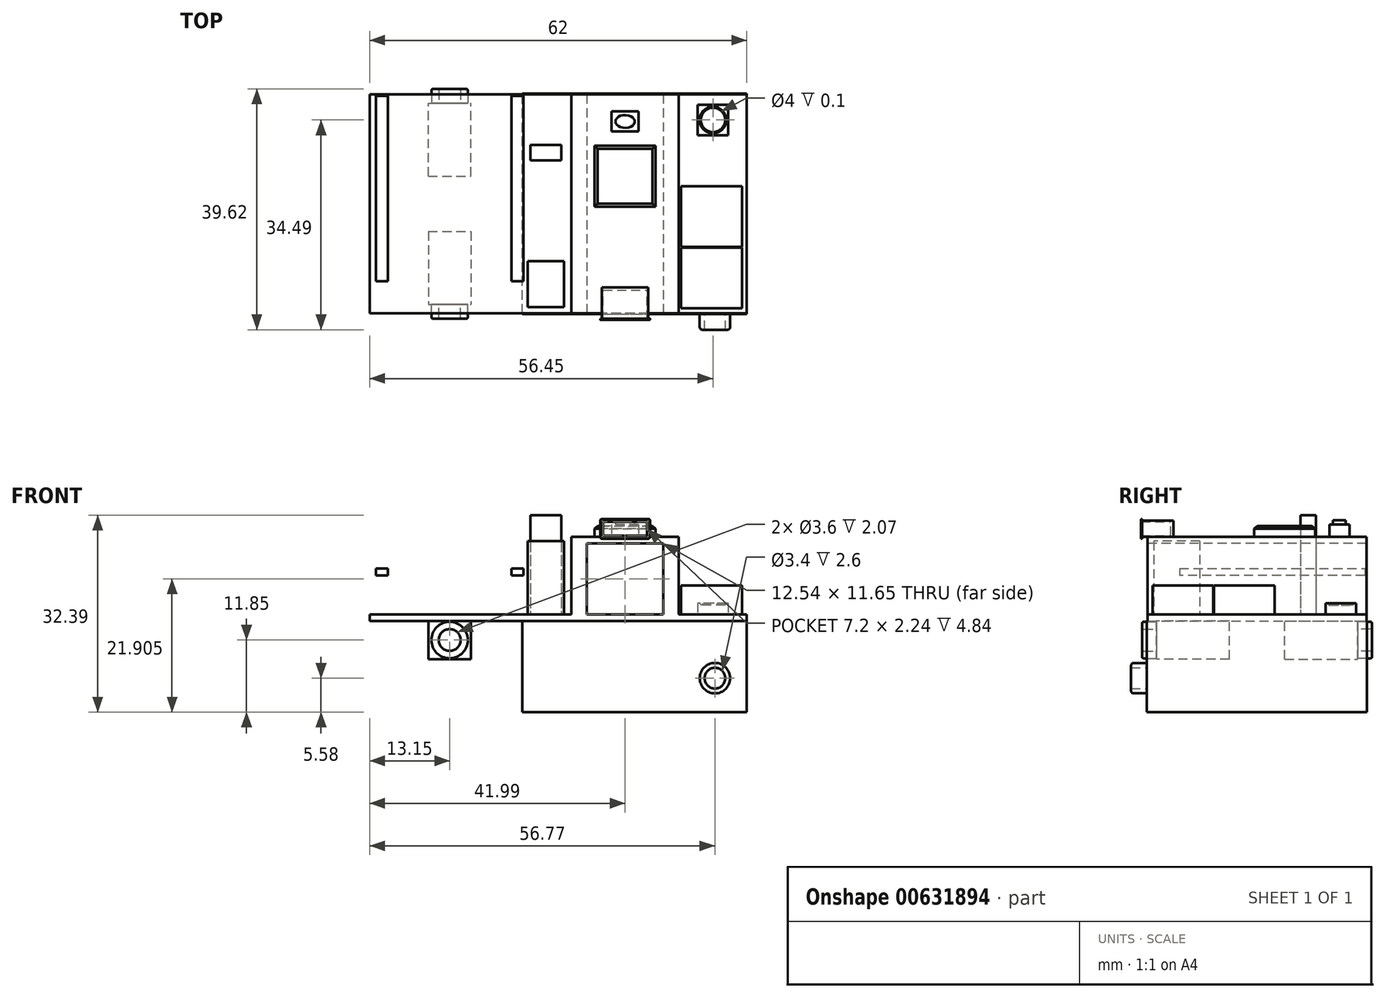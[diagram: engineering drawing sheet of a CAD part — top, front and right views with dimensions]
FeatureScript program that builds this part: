
annotation { "Feature Type Name" : "Feature", "Feature Type Description" : "" }
export const myFeature = defineFeature(function(context is Context, id is Id, definition is map)
    precondition{}
    {
        {
            assignVariable(context, id + "F0", {"name" : "epaisseur", "anyValue" : 1.08});
        }
        {
            var Q0;
            Q0=qCreatedBy(makeId("Top.planeOp"),FACE);
            var sketch = newSketch(context, id + "F1", { "sketchPlane" : qUnion([Q0])});
            skLineSegment(sketch, "E0.bottom", {"start": v(31, -18) * mm, "end": v(-31, -18) * mm});
            skLineSegment(sketch, "E0.top", {"start": v(31, 18) * mm, "end": v(-31, 18) * mm});
            skLineSegment(sketch, "E0.left", {"start": v(31, -18) * mm, "end": v(31, 18) * mm});
            skLineSegment(sketch, "E0.right", {"start": v(-31, -18) * mm, "end": v(-31, 18) * mm});
            skPoint(sketch, "E0.middle", {"position": v(0, 0) * mm});
            skSolve(sketch);
        }
        {
            var Q0;
            Q0=qSketchRegion(id+"F1",true);
            extrude(context, id + "F2", {"entities" : qUnion([Q0]), "depth" : (getVariable(context, 'epaisseur') / 2) * mm, "offsetDistance" : 25 * mm, "hasSecondDirection" : true, "secondDirectionOppositeDirection" : true, "secondDirectionDepth" : (getVariable(context, 'epaisseur') / 2) * mm});
        }
        {
            var Q0;
            Q0=makeQuery(id+"F2.opExtrude","CAP_FACE",FACE,{"disambiguationData":[OSD([sQuery(id+"F1.wireOp",EDGE,"E0.bottom"),sQuery(id+"F1.wireOp",EDGE,"E0.top"),sQuery(id+"F1.wireOp",EDGE,"E0.left"),sQuery(id+"F1.wireOp",EDGE,"E0.right")])],"isStart":false});
            var sketch = newSketch(context, id + "F3", { "sketchPlane" : qUnion([Q0])});
            skLineSegment(sketch, "E1.bottom", {"start": v(27.95, 11.3) * mm, "end": v(22.95, 11.3) * mm});
            skLineSegment(sketch, "E1.top", {"start": v(27.95, 16.3) * mm, "end": v(22.95, 16.3) * mm});
            skLineSegment(sketch, "E1.left", {"start": v(27.95, 11.3) * mm, "end": v(27.95, 16.3) * mm});
            skLineSegment(sketch, "E1.right", {"start": v(22.95, 11.3) * mm, "end": v(22.95, 16.3) * mm});
            skPoint(sketch, "E1.middle", {"position": v(25.45, 13.8) * mm});
            skCircle(sketch, "E2", {"center": v(25.45, 13.8) * mm, "radius": 2 * mm});
            skLineSegment(sketch, "E3.bottom", {"start": v(19.8, -18) * mm, "end": v(2.18, -18) * mm});
            skLineSegment(sketch, "E3.top", {"start": v(19.8, 18) * mm, "end": v(2.18, 18) * mm});
            skLineSegment(sketch, "E3.left", {"start": v(19.8, -18) * mm, "end": v(19.8, 18) * mm});
            skLineSegment(sketch, "E3.right", {"start": v(2.18, -18) * mm, "end": v(2.18, 18) * mm});
            skLineSegment(sketch, "E4", {"start": v(4.72, 18) * mm, "end": v(4.72, -18) * mm});
            skLineSegment(sketch, "E5", {"start": v(17.26, 18) * mm, "end": v(17.26, -18) * mm});
            skLineSegment(sketch, "E6.bottom", {"start": v(30.2, 2.9) * mm, "end": v(20.2, 2.9) * mm});
            skLineSegment(sketch, "E6.top", {"start": v(30.2, -7.1) * mm, "end": v(20.2, -7.1) * mm});
            skLineSegment(sketch, "E6.left", {"start": v(30.2, 2.9) * mm, "end": v(30.2, -7.1) * mm});
            skLineSegment(sketch, "E6.right", {"start": v(20.2, 2.9) * mm, "end": v(20.2, -7.1) * mm});
            skLineSegment(sketch, "E7.1.0.0", {"start": v(30.2, -7.2) * mm, "end": v(20.2, -7.2) * mm});
            skLineSegment(sketch, "E7.1.0.1", {"start": v(30.2, -17.2) * mm, "end": v(20.2, -17.2) * mm});
            skLineSegment(sketch, "E7.1.0.2", {"start": v(30.2, -7.2) * mm, "end": v(30.2, -17.2) * mm});
            skLineSegment(sketch, "E7.1.0.3", {"start": v(20.2, -7.2) * mm, "end": v(20.2, -17.2) * mm});
            skLineSegment(sketch, "E7.direction1", {"start": v(20.2, -7.1) * mm, "end": v(20.2, -17.2) * mm, "construction": true});
            skLineSegment(sketch, "E8", {"start": v(-30, 17.75) * mm, "end": v(-5.7, 17.75) * mm});
            skLineSegment(sketch, "E9", {"start": v(-5.7, 17.75) * mm, "end": v(-5.7, -12.75) * mm});
            skLineSegment(sketch, "E10", {"start": v(-5.7, -12.75) * mm, "end": v(-13.35, -17.75) * mm});
            skLineSegment(sketch, "E11", {"start": v(-13.35, -17.75) * mm, "end": v(-22.35, -17.75) * mm});
            skLineSegment(sketch, "E12", {"start": v(-22.35, -17.75) * mm, "end": v(-30, -12.75) * mm});
            skLineSegment(sketch, "E13", {"start": v(-30, -12.75) * mm, "end": v(-30, 17.75) * mm});
            skLineSegment(sketch, "E14.bottom", {"start": v(-30, 17.75) * mm, "end": v(-28, 17.75) * mm});
            skLineSegment(sketch, "E14.top", {"start": v(-30, -12.75) * mm, "end": v(-28, -12.75) * mm});
            skLineSegment(sketch, "E14.left", {"start": v(-30, 17.75) * mm, "end": v(-30, -12.75) * mm});
            skLineSegment(sketch, "E14.right", {"start": v(-28, 17.75) * mm, "end": v(-28, -12.75) * mm});
            skLineSegment(sketch, "E15.bottom", {"start": v(-5.7, 17.75) * mm, "end": v(-7.7, 17.75) * mm});
            skLineSegment(sketch, "E15.top", {"start": v(-5.7, -12.75) * mm, "end": v(-7.7, -12.75) * mm});
            skLineSegment(sketch, "E15.right", {"start": v(-7.7, 17.75) * mm, "end": v(-7.7, -12.75) * mm});
            skLineSegment(sketch, "E16.bottom", {"start": v(-5.02, -9.4) * mm, "end": v(0.98, -9.4) * mm});
            skLineSegment(sketch, "E16.top", {"start": v(-5.02, -17) * mm, "end": v(0.98, -17) * mm});
            skLineSegment(sketch, "E16.left", {"start": v(-5.02, -9.4) * mm, "end": v(-5.02, -17) * mm});
            skLineSegment(sketch, "E16.right", {"start": v(0.98, -9.4) * mm, "end": v(0.98, -17) * mm});
            skCircle(sketch, "E17", {"center": v(-1.12, 15.47) * mm, "radius": 2 * mm});
            skLineSegment(sketch, "E18.bottom", {"start": v(-4.55, 9.7) * mm, "end": v(0.53, 9.7) * mm});
            skLineSegment(sketch, "E18.top", {"start": v(-4.55, 7.15) * mm, "end": v(0.53, 7.15) * mm});
            skLineSegment(sketch, "E18.left", {"start": v(-4.55, 9.7) * mm, "end": v(-4.55, 7.15) * mm});
            skLineSegment(sketch, "E18.right", {"start": v(0.53, 9.7) * mm, "end": v(0.53, 7.15) * mm});
            skSolve(sketch);
        }
        {
            var Q0;
            Q0=makeQuery(id+"F3.imprint","IMPRINT",FACE,{"disambiguationData":[TD([[makeQuery(id+"F3.imprint","IMPRINT",EDGE,{"derivedFrom":sQuery(id+"F3.wireOp",EDGE,"E1.bottom")}),-1.0]])]});
            var Q1;
            Q1=makeQuery(id+"F3.imprint","IMPRINT",FACE,{"disambiguationData":[TD([[makeQuery(id+"F3.imprint","IMPRINT",EDGE,{"derivedFrom":sQuery(id+"F3.wireOp",EDGE,"46dbcd92-cdc2-429d-924f-770beef507a0.1.1.0")}),-1.0]])]});
            var Q2;
            Q2=makeQuery(id+"F3.imprint","IMPRINT",FACE,{"disambiguationData":[TD([[makeQuery(id+"F3.imprint","IMPRINT",EDGE,{"derivedFrom":sQuery(id+"F3.wireOp",EDGE,"25c404a9-2ccf-4400-a537-ff987a43f8d3.1.0.0")}),-1.0]])]});
            var Q3;
            Q3=makeQuery(id+"F3.imprint","IMPRINT",FACE,{"disambiguationData":[TD([[makeQuery(id+"F3.imprint","IMPRINT",EDGE,{"derivedFrom":sQuery(id+"F3.wireOp",EDGE,"5cae1187-fbfc-416b-a3f4-cd89fc04e58b.1.0.1")}),1.0]])]});
            var Q4;
            Q4=makeQuery(id+"F3.imprint","IMPRINT",FACE,{"disambiguationData":[TD([[makeQuery(id+"F3.imprint","IMPRINT",EDGE,{"derivedFrom":sQuery(id+"F3.wireOp",EDGE,"5cae1187-fbfc-416b-a3f4-cd89fc04e58b.1.0.7")}),-1.0]])]});
            extrude(context, id + "F4", {"entities" : qUnion([Q0, Q1, Q2, Q3, Q4]), "operationType" : NewBodyOperationType.ADD, "depth" : 1.8 * mm, "offsetDistance" : 25 * mm});
        }
        {
            var Q0;
            Q0=makeQuery(id+"F3.imprint","IMPRINT",FACE,{"disambiguationData":[TD([[makeQuery(id+"F3.imprint","IMPRINT",EDGE,{"derivedFrom":sQuery(id+"F3.wireOp",EDGE,"25c404a9-2ccf-4400-a537-ff987a43f8d3.1.0.4")}),1.0]])]});
            var Q1;
            Q1=makeQuery(id+"F3.imprint","IMPRINT",FACE,{"disambiguationData":[TD([[makeQuery(id+"F3.imprint","IMPRINT",EDGE,{"derivedFrom":sQuery(id+"F3.wireOp",EDGE,"46dbcd92-cdc2-429d-924f-770beef507a0.13.1.0")}),1.0]])]});
            var Q2;
            Q2=makeQuery(id+"F3.imprint","IMPRINT",FACE,{"disambiguationData":[TD([[makeQuery(id+"F3.imprint","IMPRINT",EDGE,{"derivedFrom":sQuery(id+"F3.wireOp",EDGE,"5cae1187-fbfc-416b-a3f4-cd89fc04e58b.1.0.6")}),1.0]])]});
            var Q3;
            Q3=makeQuery(id+"F3.imprint","IMPRINT",FACE,{"disambiguationData":[TD([[makeQuery(id+"F3.imprint","IMPRINT",EDGE,{"derivedFrom":sQuery(id+"F3.wireOp",EDGE,"5cae1187-fbfc-416b-a3f4-cd89fc04e58b.1.0.10")}),1.0]])]});
            var Q4;
            Q4=makeQuery(id+"F3.imprint","IMPRINT",FACE,{"disambiguationData":[TD([[makeQuery(id+"F3.imprint","IMPRINT",EDGE,{"derivedFrom":sQuery(id+"F3.wireOp",EDGE,"E2")}),1.0]])]});
            extrude(context, id + "F5", {"entities" : qUnion([Q0, Q1, Q2, Q3, Q4]), "operationType" : NewBodyOperationType.ADD, "depth" : 1.5 * mm, "offsetDistance" : 25 * mm});
        }
        {
            var Q0;
            Q0=makeQuery(id+"F4.opExtrude","CAP_EDGE",EDGE,{"disambiguationData":[OSD([sQuery(id+"F3.wireOp",EDGE,"5cae1187-fbfc-416b-a3f4-cd89fc04e58b.1.0.6")])],"isStart":false});
            var Q1;
            Q1=makeQuery(id+"F4.opExtrude","CAP_EDGE",EDGE,{"disambiguationData":[OSD([sQuery(id+"F3.wireOp",EDGE,"5cae1187-fbfc-416b-a3f4-cd89fc04e58b.1.0.10")])],"isStart":false});
            var Q2;
            Q2=makeQuery(id+"F4.opExtrude","CAP_EDGE",EDGE,{"disambiguationData":[OSD([sQuery(id+"F3.wireOp",EDGE,"E2")])],"isStart":false});
            var Q3;
            Q3=makeQuery(id+"F4.opExtrude","CAP_EDGE",EDGE,{"disambiguationData":[OSD([sQuery(id+"F3.wireOp",EDGE,"25c404a9-2ccf-4400-a537-ff987a43f8d3.1.0.4")])],"isStart":false});
            var Q4;
            Q4=makeQuery(id+"F4.opExtrude","CAP_EDGE",EDGE,{"disambiguationData":[OSD([sQuery(id+"F3.wireOp",EDGE,"46dbcd92-cdc2-429d-924f-770beef507a0.13.1.0")])],"isStart":false});
            chamfer(context, id + "F6", {"entities" : qUnion([Q0, Q1, Q2, Q3, Q4]), "width" : 0.2 * mm, "tangentPropagation" : true});
        }
        {
            var Q0;
            {var subQ0=sQuery(id+"F3.wireOp",EDGE,"E3.right");Q0=makeQuery(id+"F3.imprint","IMPRINT",FACE,{"disambiguationData":[TD([[makeQuery(id+"F3.imprint","IMPRINT",EDGE,{"derivedFrom":subQ0}),-1.0]])]});}
            var Q1;
            {var subQ0=sQuery(id+"F3.wireOp",EDGE,"fOPfJSet-owwX-ZUtX-Vyne-BZuTA3JeBzhn");Q1=makeQuery(id+"F3.imprint","IMPRINT",FACE,{"disambiguationData":[TD([[makeQuery(id+"F3.imprint","IMPRINT",EDGE,{"derivedFrom":subQ0}),1.0]])]});}
            var Q2;
            {var subQ0=sQuery(id+"F3.wireOp",EDGE,"E3.left");Q2=makeQuery(id+"F3.imprint","IMPRINT",FACE,{"disambiguationData":[TD([[makeQuery(id+"F3.imprint","IMPRINT",EDGE,{"derivedFrom":subQ0}),1.0]])]});}
            var Q3;
            {var subQ0=sQuery(id+"F3.wireOp",EDGE,"E4");Q3=makeQuery(id+"F3.imprint","IMPRINT",FACE,{"disambiguationData":[TD([[makeQuery(id+"F3.imprint","IMPRINT",EDGE,{"derivedFrom":subQ0}),1.0]])]});}
            extrude(context, id + "F7", {"entities" : qUnion([Q0, Q1, Q2, Q3]), "operationType" : NewBodyOperationType.ADD, "depth" : 12.75 * mm, "offsetDistance" : 25 * mm});
        }
        {
            var Q0;
            {var subQ0=sQuery(id+"F3.wireOp",EDGE,"E4");Q0=makeQuery(id+"F3.imprint","IMPRINT",FACE,{"disambiguationData":[TD([[makeQuery(id+"F3.imprint","IMPRINT",EDGE,{"derivedFrom":subQ0}),1.0]])]});}
            var Q1;
            Q1=makeQuery(id+"F7.opExtrude","CAP_FACE",FACE,{"disambiguationData":[OSD([sQuery(id+"F3.wireOp",EDGE,"E3.bottom"),sQuery(id+"F3.wireOp",EDGE,"E3.top"),sQuery(id+"F3.wireOp",EDGE,"E3.left"),sQuery(id+"F3.wireOp",EDGE,"E3.right")])],"isStart":false});
            extrude(context, id + "F8", {"entities" : qUnion([Q0]), "operationType" : NewBodyOperationType.REMOVE, "endBound" : BoundingType.UP_TO_SURFACE, "depth" : 25 * mm, "endBoundEntityFace" : qUnion([Q1]), "hasOffset" : true, "offsetDistance" : 1.1 * mm});
        }
        {
            var Q0;
            Q0=makeQuery(id+"F3.imprint","IMPRINT",FACE,{"disambiguationData":[TD([[makeQuery(id+"F3.imprint","IMPRINT",EDGE,{"derivedFrom":sQuery(id+"F3.wireOp",EDGE,"E7.1.0.0")}),1.0]])]});
            var Q1;
            Q1=makeQuery(id+"F3.imprint","IMPRINT",FACE,{"disambiguationData":[TD([[makeQuery(id+"F3.imprint","IMPRINT",EDGE,{"derivedFrom":sQuery(id+"F3.wireOp",EDGE,"E6.bottom")}),1.0]])]});
            extrude(context, id + "F9", {"entities" : qUnion([Q0, Q1]), "operationType" : NewBodyOperationType.ADD, "depth" : 4.75 * mm, "offsetDistance" : 25 * mm});
        }
        {
            var Q0;
            Q0=makeQuery(id+"F3.imprint","IMPRINT",FACE,{"disambiguationData":[TD([[makeQuery(id+"F3.imprint","IMPRINT",EDGE,{"derivedFrom":sQuery(id+"F3.wireOp",EDGE,"E14.bottom")}),-1.0]])]});
            var Q1;
            Q1=makeQuery(id+"F3.imprint","IMPRINT",FACE,{"disambiguationData":[TD([[makeQuery(id+"F3.imprint","IMPRINT",EDGE,{"derivedFrom":sQuery(id+"F3.wireOp",EDGE,"E8")}),-1.0]])]});
            var Q2;
            Q2=makeQuery(id+"F3.imprint","IMPRINT",FACE,{"disambiguationData":[TD([[makeQuery(id+"F3.imprint","IMPRINT",EDGE,{"derivedFrom":sQuery(id+"F3.wireOp",EDGE,"E15.bottom")}),1.0]])]});
            extrude(context, id + "F10", {"entities" : qUnion([Q0, Q1, Q2]), "operationType" : NewBodyOperationType.ADD, "depth" : 7.5 * mm, "offsetDistance" : 25 * mm});
        }
        {
            var Q0;
            Q0=makeQuery(id+"F3.imprint","IMPRINT",FACE,{"disambiguationData":[TD([[makeQuery(id+"F3.imprint","IMPRINT",EDGE,{"derivedFrom":sQuery(id+"F3.wireOp",EDGE,"E8")}),-1.0]])]});
            var Q1;
            Q1=makeQuery(id+"F10.opExtrude","CAP_FACE",FACE,{"disambiguationData":[OSD([sQuery(id+"F3.wireOp",EDGE,"E8"),sQuery(id+"F3.wireOp",EDGE,"E10"),sQuery(id+"F3.wireOp",EDGE,"E11"),sQuery(id+"F3.wireOp",EDGE,"E12"),sQuery(id+"F3.wireOp",EDGE,"E14.bottom"),sQuery(id+"F3.wireOp",EDGE,"E14.left"),sQuery(id+"F3.wireOp",EDGE,"E15.bottom"),sQuery(id+"F3.wireOp",EDGE,"E9")])],"isStart":false});
            extrude(context, id + "F11", {"entities" : qUnion([Q0]), "operationType" : NewBodyOperationType.REMOVE, "endBound" : BoundingType.UP_TO_SURFACE, "depth" : 25 * mm, "endBoundEntityFace" : qUnion([Q1]), "hasOffset" : true, "offsetDistance" : 1.1 * mm});
        }
        {
            var Q0;
            Q0=makeQuery(id+"F3.imprint","IMPRINT",FACE,{"disambiguationData":[TD([[makeQuery(id+"F3.imprint","IMPRINT",EDGE,{"derivedFrom":sQuery(id+"F3.wireOp",EDGE,"E18.bottom")}),-1.0]])]});
            extrude(context, id + "F12", {"entities" : qUnion([Q0]), "operationType" : NewBodyOperationType.ADD, "depth" : 16.3 * mm, "offsetDistance" : 25 * mm});
        }
        {
            var Q0;
            Q0=makeQuery(id+"F3.imprint","IMPRINT",FACE,{"disambiguationData":[TD([[makeQuery(id+"F3.imprint","IMPRINT",EDGE,{"derivedFrom":sQuery(id+"F3.wireOp",EDGE,"E16.bottom")}),-1.0]])]});
            extrude(context, id + "F13", {"entities" : qUnion([Q0]), "operationType" : NewBodyOperationType.ADD, "depth" : (17.12 - 5.08) * mm, "offsetDistance" : 25 * mm});
        }
        {
            var Q0;
            Q0=makeQuery(id+"F7.opExtrude","CAP_FACE",FACE,{"disambiguationData":[OSD([sQuery(id+"F3.wireOp",EDGE,"E3.bottom"),sQuery(id+"F3.wireOp",EDGE,"E3.top"),sQuery(id+"F3.wireOp",EDGE,"E3.left"),sQuery(id+"F3.wireOp",EDGE,"E3.right")])],"isStart":false});
            var sketch = newSketch(context, id + "F14", { "sketchPlane" : qUnion([Q0])});
            skLineSegment(sketch, "E19.bottom", {"start": v(14.8, -18.86) * mm, "end": v(7.2, -18.86) * mm});
            skLineSegment(sketch, "E19.top", {"start": v(14.8, -13.72) * mm, "end": v(7.2, -13.72) * mm});
            skLineSegment(sketch, "E19.left", {"start": v(14.8, -18.86) * mm, "end": v(14.8, -13.72) * mm});
            skLineSegment(sketch, "E19.right", {"start": v(7.2, -18.86) * mm, "end": v(7.2, -13.72) * mm});
            skPoint(sketch, "E19.middle", {"position": v(11, -16.29) * mm});
            skPoint(sketch, "E19.middle.positionSnap0", {"position": v(11, -18) * mm});
            skPoint(sketch, "E19.centerSnap0", {"position": v(11, -18) * mm});
            skLineSegment(sketch, "E20.bottom", {"start": v(13.2, 11.9) * mm, "end": v(8.8, 11.9) * mm});
            skLineSegment(sketch, "E20.top", {"start": v(13.2, 15.2) * mm, "end": v(8.8, 15.2) * mm});
            skLineSegment(sketch, "E20.left", {"start": v(13.2, 11.9) * mm, "end": v(13.2, 15.2) * mm});
            skLineSegment(sketch, "E20.right", {"start": v(8.8, 11.9) * mm, "end": v(8.8, 15.2) * mm});
            skPoint(sketch, "E20.middle", {"position": v(11, 13.55) * mm});
            skLineSegment(sketch, "E21.bottom", {"start": v(16, -0.45) * mm, "end": v(6, -0.45) * mm});
            skLineSegment(sketch, "E21.top", {"start": v(16, 9.55) * mm, "end": v(6, 9.55) * mm});
            skLineSegment(sketch, "E21.left", {"start": v(16, -0.45) * mm, "end": v(16, 9.55) * mm});
            skLineSegment(sketch, "E21.right", {"start": v(6, -0.45) * mm, "end": v(6, 9.55) * mm});
            skPoint(sketch, "E21.middle", {"position": v(11, 4.55) * mm});
            skEllipse(sketch, "E22", {"center": v(11, 13.55) * mm, "majorRadius": 1.05 * mm, "minorRadius": 1.6 * mm, "majorAxis": v(0, 1)});
            skSolve(sketch);
        }
        {
            var Q0;
            Q0=makeQuery(id+"F14.imprint","IMPRINT",FACE,{"disambiguationData":[TD([[makeQuery(id+"F14.imprint","IMPRINT",EDGE,{"derivedFrom":sQuery(id+"F14.wireOp",EDGE,"E21.bottom")}),-1.0]])]});
            extrude(context, id + "F15", {"entities" : qUnion([Q0]), "operationType" : NewBodyOperationType.ADD, "depth" : 1.8 * mm, "offsetDistance" : 25 * mm});
        }
        {
            var Q0;
            Q0=makeQuery(id+"F15.opExtrude","CAP_FACE",FACE,{"disambiguationData":[OSD([sQuery(id+"F14.wireOp",EDGE,"E21.bottom"),sQuery(id+"F14.wireOp",EDGE,"E21.top"),sQuery(id+"F14.wireOp",EDGE,"E21.left"),sQuery(id+"F14.wireOp",EDGE,"E21.right")])],"isStart":false});
            chamfer(context, id + "F16", {"entities" : qUnion([Q0]), "width" : 0.5 * mm, "tangentPropagation" : true});
        }
        {
            var Q0;
            {var subQ0=sQuery(id+"F14.wireOp",EDGE,"E19.bottom");Q0=makeQuery(id+"F14.imprint","IMPRINT",FACE,{"disambiguationData":[TD([[makeQuery(id+"F14.imprint","IMPRINT",EDGE,{"derivedFrom":subQ0}),-1.0]])]});}
            var Q1;
            {var subQ0=sQuery(id+"F14.wireOp",EDGE,"E19.top");Q1=makeQuery(id+"F14.imprint","IMPRINT",FACE,{"disambiguationData":[TD([[makeQuery(id+"F14.imprint","IMPRINT",EDGE,{"derivedFrom":subQ0}),1.0]])]});}
            extrude(context, id + "F17", {"entities" : qUnion([Q0, Q1]), "depth" : 2.64 * mm, "offsetDistance" : 25 * mm});
        }
        {
            var Q0;
            Q0=makeQuery(id+"F17.opExtrude","SWEPT_FACE",FACE,{"disambiguationData":[OSD([sQuery(id+"F14.wireOp",EDGE,"E19.bottom")])]});
            var sketch = newSketch(context, id + "F18", { "sketchPlane" : qUnion([Q0])});
            skLineSegment(sketch, "E23.0", {"start": v(14.8, 15.93) * mm, "end": v(7.2, 15.93) * mm, "construction": true});
            skLineSegment(sketch, "E23.1", {"start": v(7.2, 15.93) * mm, "end": v(7.2, 13.3) * mm, "construction": true});
            skLineSegment(sketch, "E23.2", {"start": v(14.8, 13.3) * mm, "end": v(7.2, 13.3) * mm, "construction": true});
            skLineSegment(sketch, "E23.3", {"start": v(14.8, 15.93) * mm, "end": v(14.8, 13.3) * mm, "construction": true});
            skLineSegment(sketch, "E24.0", {"start": v(6.9, 15.93) * mm, "end": v(6.9, 13.29) * mm});
            skLineSegment(sketch, "E24.1", {"start": v(14.8, 16.23) * mm, "end": v(7.2, 16.23) * mm});
            skLineSegment(sketch, "E24.2", {"start": v(15.1, 15.93) * mm, "end": v(15.1, 13.29) * mm});
            skLineSegment(sketch, "E24.3", {"start": v(14.8, 13) * mm, "end": v(7.2, 13) * mm});
            skPoint(sketch, "E25.visualSharp", {"position": v(6.9, 16.23) * mm});
            skArc(sketch, "E25.filletArc", {"start": v(7.2, 16.23) * mm, "mid": v(6.98, 16.14) * mm, "end": v(6.9, 15.93) * mm});
            skPoint(sketch, "E26.visualSharp", {"position": v(15.1, 16.23) * mm});
            skArc(sketch, "E26.filletArc", {"start": v(15.1, 15.93) * mm, "mid": v(15, 16.14) * mm, "end": v(14.8, 16.23) * mm});
            skPoint(sketch, "E27.visualSharp", {"position": v(15.1, 13) * mm});
            skArc(sketch, "E27.filletArc", {"start": v(14.8, 13) * mm, "mid": v(15, 13.08) * mm, "end": v(15.1, 13.29) * mm});
            skPoint(sketch, "E28.visualSharp", {"position": v(6.9, 13) * mm});
            skArc(sketch, "E28.filletArc", {"start": v(6.9, 13.29) * mm, "mid": v(6.98, 13.08) * mm, "end": v(7.2, 13) * mm});
            skLineSegment(sketch, "E29.0", {"start": v(14.6, 15.73) * mm, "end": v(7.39, 15.73) * mm});
            skLineSegment(sketch, "E29.1", {"start": v(14.6, 15.73) * mm, "end": v(14.6, 13.49) * mm});
            skLineSegment(sketch, "E29.2", {"start": v(14.6, 13.49) * mm, "end": v(7.39, 13.49) * mm});
            skLineSegment(sketch, "E29.3", {"start": v(7.39, 15.73) * mm, "end": v(7.39, 13.49) * mm});
            skSolve(sketch);
        }
        {
            var Q0;
            Q0=qSketchRegion(id+"F18",true);
            var Q1;
            Q1=makeQuery(id+"F18.imprint","IMPRINT",FACE,{"disambiguationData":[TD([[makeQuery(id+"F18.imprint","IMPRINT",EDGE,{"derivedFrom":sQuery(id+"F18.wireOp",EDGE,"E23.0")}),1.0]])]});
            extrude(context, id + "F19", {"entities" : qUnion([Q0, Q1]), "operationType" : NewBodyOperationType.ADD, "depth" : 0.2 * mm, "offsetDistance" : 25 * mm});
        }
        {
            var Q0;
            Q0=makeQuery(id+"F18.imprint","IMPRINT",FACE,{"disambiguationData":[TD([[makeQuery(id+"F18.imprint","IMPRINT",EDGE,{"derivedFrom":sQuery(id+"F18.wireOp",EDGE,"E29.0")}),1.0]])]});
            var Q1;
            Q1=makeQuery(id+"F17.opExtrude","SWEPT_FACE",FACE,{"disambiguationData":[OSD([sQuery(id+"F14.wireOp",EDGE,"E19.top")])]});
            extrude(context, id + "F20", {"entities" : qUnion([Q0]), "operationType" : NewBodyOperationType.REMOVE, "endBound" : BoundingType.UP_TO_SURFACE, "oppositeDirection" : true, "depth" : 25 * mm, "endBoundEntityFace" : qUnion([Q1]), "hasOffset" : true, "offsetDistance" : 0.5 * mm});
        }
        {
            var Q0;
            Q0=makeQuery(id+"F14.imprint","IMPRINT",FACE,{"disambiguationData":[TD([[makeQuery(id+"F14.imprint","IMPRINT",EDGE,{"derivedFrom":sQuery(id+"F14.wireOp",EDGE,"E20.bottom")}),-1.0]])]});
            extrude(context, id + "F21", {"entities" : qUnion([Q0]), "operationType" : NewBodyOperationType.ADD, "depth" : 2 * mm, "offsetDistance" : 25 * mm});
        }
        {
            var Q0;
            Q0=makeQuery(id+"F14.imprint","IMPRINT",FACE,{"disambiguationData":[TD([[makeQuery(id+"F14.imprint","IMPRINT",EDGE,{"derivedFrom":sQuery(id+"F14.wireOp",EDGE,"E22")}),1.0]])]});
            extrude(context, id + "F22", {"entities" : qUnion([Q0]), "operationType" : NewBodyOperationType.ADD, "depth" : 2.7 * mm, "offsetDistance" : 25 * mm});
        }
        {
            var Q0;
            Q0=makeQuery(id+"F2.opExtrude","CAP_FACE",FACE,{"disambiguationData":[OSD([sQuery(id+"F1.wireOp",EDGE,"E0.bottom"),sQuery(id+"F1.wireOp",EDGE,"E0.top"),sQuery(id+"F1.wireOp",EDGE,"E0.left"),sQuery(id+"F1.wireOp",EDGE,"E0.right")])],"isStart":true});
            var sketch = newSketch(context, id + "F23", { "sketchPlane" : qUnion([Q0])});
            skLineSegment(sketch, "E30.bottom", {"start": v(-21.35, -4.55) * mm, "end": v(-14.35, -4.55) * mm});
            skLineSegment(sketch, "E30.top", {"start": v(-21.35, -16.55) * mm, "end": v(-14.35, -16.55) * mm});
            skLineSegment(sketch, "E30.left", {"start": v(-21.35, -4.55) * mm, "end": v(-21.35, -16.55) * mm});
            skLineSegment(sketch, "E30.right", {"start": v(-14.35, -4.55) * mm, "end": v(-14.35, -16.55) * mm});
            skPoint(sketch, "E31", {"position": v(-17.85, -16.55) * mm});
            skPoint(sketch, "E32.0", {"position": v(-17.85, -17.75) * mm});
            skLineSegment(sketch, "E33.bottom", {"start": v(-5.92, 18.1) * mm, "end": v(31, 18.1) * mm});
            skLineSegment(sketch, "E33.top", {"start": v(-5.92, -18.1) * mm, "end": v(31, -18.1) * mm});
            skLineSegment(sketch, "E33.left", {"start": v(-5.92, 18.1) * mm, "end": v(-5.92, -18.1) * mm});
            skLineSegment(sketch, "E33.right", {"start": v(31, 18.1) * mm, "end": v(31, -18.1) * mm});
            skPoint(sketch, "E34", {"position": v(12.54, 0) * mm});
            skPoint(sketch, "E34.positionSnap0", {"position": v(-5.92, 0) * mm});
            skPoint(sketch, "E34.positionSnap1", {"position": v(12.54, 18.1) * mm});
            skSolve(sketch);
        }
        {
            var Q0;
            {var subQ0=sQuery(id+"F23.wireOp",EDGE,"E33.bottom");Q0=makeQuery(id+"F23.imprint","IMPRINT",FACE,{"disambiguationData":[TD([[makeQuery(id+"F23.imprint","IMPRINT",EDGE,{"derivedFrom":subQ0}),-1.0]])]});}
            var Q1;
            {var subQ0=sQuery(id+"F23.wireOp",EDGE,"E33.top");Q1=makeQuery(id+"F23.imprint","IMPRINT",FACE,{"disambiguationData":[TD([[makeQuery(id+"F23.imprint","IMPRINT",EDGE,{"derivedFrom":subQ0}),1.0]])]});}
            var Q2;
            {var subQ0=sQuery(id+"F23.wireOp",EDGE,"E33.left");var subQ1=makeQuery(id+"F2.opExtrude","CAP_EDGE",EDGE,{"disambiguationData":[OSD([sQuery(id+"F1.wireOp",EDGE,"E0.bottom")])],"isStart":true});var subQ2=makeQuery(id+"F23.imprint","INTERSECT",VERTEX,{"derivedFrom":[subQ1,subQ0]});Q2=makeQuery(id+"F23.imprint","IMPRINT",FACE,{"disambiguationData":[TD([[makeQuery(id+"F23.imprint","IMPRINT",EDGE,{"disambiguationData":[TD([[subQ2,-1.0]])],"derivedFrom":subQ0}),1.0]])]});}
            extrude(context, id + "F24", {"entities" : qUnion([Q0, Q1, Q2]), "operationType" : NewBodyOperationType.ADD, "depth" : 15 * mm, "offsetDistance" : 25 * mm});
        }
        {
            var Q0;
            Q0=makeQuery(id+"F23.imprint","IMPRINT",FACE,{"disambiguationData":[TD([[makeQuery(id+"F23.imprint","IMPRINT",EDGE,{"derivedFrom":sQuery(id+"F23.wireOp",EDGE,"E30.bottom")}),-1.0]])]});
            extrude(context, id + "F25", {"entities" : qUnion([Q0]), "depth" : 6.3 * mm, "offsetDistance" : 25 * mm});
        }
        {
            var Q0;
            Q0=makeQuery(id+"F25.opExtrude","SWEPT_FACE",FACE,{"disambiguationData":[OSD([sQuery(id+"F23.wireOp",EDGE,"E30.top")])]});
            var sketch = newSketch(context, id + "F26", { "sketchPlane" : qUnion([Q0])});
            skCircle(sketch, "E35", {"center": v(17.85, -3.69) * mm, "radius": 3 * mm});
            skLineSegment(sketch, "E36", {"start": v(21.35, -3.69) * mm, "end": v(14.35, -3.69) * mm, "construction": true});
            skLineSegment(sketch, "E37", {"start": v(17.85, -6.84) * mm, "end": v(17.85, -0.54) * mm, "construction": true});
            skCircle(sketch, "E38.0", {"center": v(17.85, -3.69) * mm, "radius": 1.8 * mm});
            skSolve(sketch);
        }
        {
            var Q0;
            Q0=qSketchRegion(id+"F26",true);
            extrude(context, id + "F27", {"entities" : qUnion([Q0]), "operationType" : NewBodyOperationType.ADD, "depth" : 2.37 * mm, "offsetDistance" : 25 * mm});
        }
        {
            var Q0;
            Q0=makeQuery(id+"F27.opExtrude","CAP_EDGE",EDGE,{"disambiguationData":[OSD([sQuery(id+"F26.wireOp",EDGE,"E38.0")])],"isStart":false});
            var Q1;
            Q1=makeQuery(id+"F27.opExtrude","CAP_EDGE",EDGE,{"disambiguationData":[OSD([sQuery(id+"F26.wireOp",EDGE,"E35")])],"isStart":false});
            fillet(context, id + "F28", {"entities" : qUnion([Q0, Q1]), "radius" : 0.3 * mm, "tangentPropagation" : true, "allowEdgeOverflow" : false});
        }
        {
            var Q0;
            Q0=makeQuery(id+"F25.opExtrude","SWEPT_BODY",BODY,{"disambiguationData":[OSD([sQuery(id+"F23.wireOp",EDGE,"E30.bottom"),sQuery(id+"F23.wireOp",EDGE,"E30.top"),sQuery(id+"F23.wireOp",EDGE,"E30.left"),sQuery(id+"F23.wireOp",EDGE,"E30.right")])]});
            var Q1;
            Q1=qCreatedBy(makeId("Front.planeOp"),FACE);
            mirror(context, id + "F29", {"entities" : qUnion([Q0]), "mirrorPlane" : qUnion([Q1])});
        }
        {
            var Q0;
            Q0=makeQuery(id+"F24.opExtrude","SWEPT_FACE",FACE,{"disambiguationData":[OSD([sQuery(id+"F23.wireOp",EDGE,"E33.bottom")])]});
            var sketch = newSketch(context, id + "F30", { "sketchPlane" : qUnion([Q0])});
            skCircle(sketch, "E39", {"center": v(25.77, -9.96) * mm, "radius": 2.5 * mm});
            skLineSegment(sketch, "E40", {"start": v(-5.92, -14.04) * mm, "end": v(31, -14.04) * mm, "construction": true});
            skCircle(sketch, "E41.0", {"center": v(25.77, -9.96) * mm, "radius": 1.7 * mm});
            skSolve(sketch);
        }
        {
            var Q0;
            Q0 = qSketchRegion(id + "F30", true);
            extrude(context, id + "F31", {"entities" : qUnion([Q0]), "operationType" : NewBodyOperationType.ADD, "depth" : 2.6 * mm, "offsetDistance" : 25 * mm});
        }
        {
            var Q0;
            Q0=makeQuery(id+"F31.opExtrude","CAP_EDGE",EDGE,{"disambiguationData":[OSD([sQuery(id+"F30.wireOp",EDGE,"E39")])],"isStart":false});
            fillet(context, id + "F32", {"entities" : qUnion([Q0]), "radius" : 0.4 * mm, "tangentPropagation" : true, "allowEdgeOverflow" : false});
        }
    });
